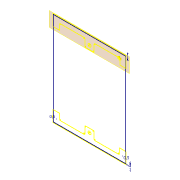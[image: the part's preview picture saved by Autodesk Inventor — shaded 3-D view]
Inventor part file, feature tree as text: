
AUTODESK INVENTOR PART (.ipt)
format: ipt  version: 2020 (Build 240168000, 168)  size: 81,408 bytes
history: native  units: mm
features: other x6, sketch x1
ambient origin geometry x8: Origin, YZ Plane, XZ Plane, XY Plane, X Axis, Y Axis, Z Axis, Center Point
feature tree (7):
  other  "Plano de trabalho1"
  sketch  "Esboço1"  dims[d0=1.0mm d1=1.0mm d2=0.5mm d3=0.5mm]
  other  "Referência1"
  other  "Referência2"
  other  "Calorímetro.iam"
  other  "suporte_fechamento:1"
  other  "suporte_fechamento:2"
